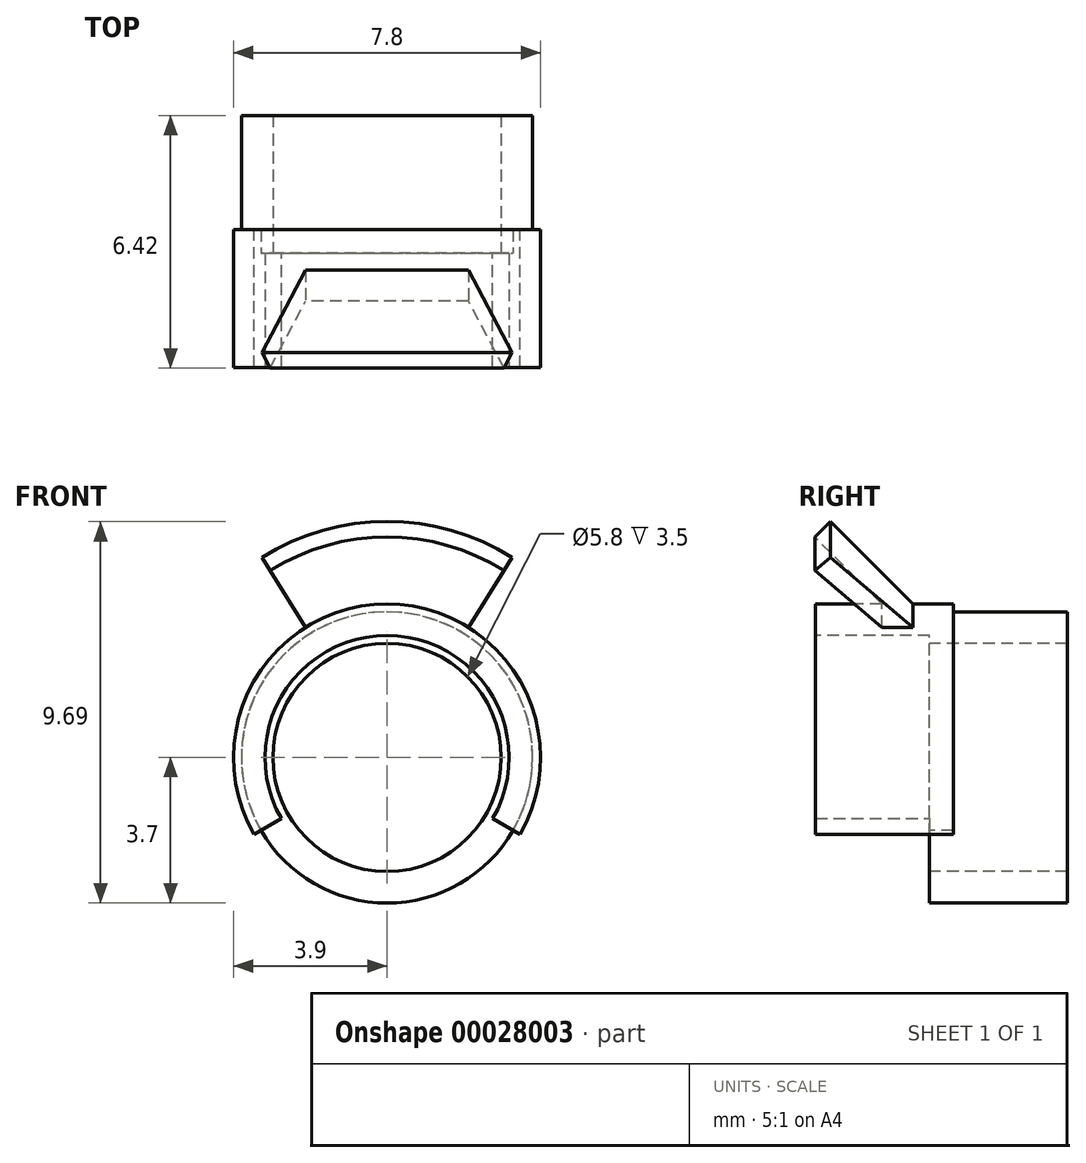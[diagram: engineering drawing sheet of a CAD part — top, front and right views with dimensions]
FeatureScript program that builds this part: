
annotation { "Feature Type Name" : "Feature", "Feature Type Description" : "" }
export const myFeature = defineFeature(function(context is Context, id is Id, definition is map)
    precondition{}
    {
        {
            var Q0;
            Q0=qCreatedBy(makeId("Right.planeOp"),FACE);
            var sketch = newSketch(context, id + "F0", { "sketchPlane" : qUnion([Q0])});
            skLineSegment(sketch, "E0.bottom", {"start": v(0.1, 3.9) * mm, "end": v(3.6, 3.9) * mm});
            skLineSegment(sketch, "E0.top", {"start": v(0.1, 3.1) * mm, "end": v(3.6, 3.1) * mm});
            skLineSegment(sketch, "E0.left", {"start": v(0.1, 3.9) * mm, "end": v(0.1, 3.1) * mm});
            skLineSegment(sketch, "E0.right", {"start": v(3.6, 3.9) * mm, "end": v(3.6, 3.1) * mm});
            skLineSegment(sketch, "E1.bottom", {"start": v(0.1, 3.1) * mm, "end": v(1.3, 3.1) * mm});
            skLineSegment(sketch, "E1.top", {"start": v(0.1, 2.3) * mm, "end": v(1.3, 2.3) * mm});
            skLineSegment(sketch, "E1.left", {"start": v(0.1, 3.1) * mm, "end": v(0.1, 2.3) * mm});
            skLineSegment(sketch, "E1.right", {"start": v(1.3, 3.1) * mm, "end": v(1.3, 2.3) * mm});
            skLineSegment(sketch, "E2", {"start": v(1.3, 3.1) * mm, "end": v(3.6, 3.1) * mm});
            skLineSegment(sketch, "E3", {"start": v(0.7, 2.3) * mm, "end": v(0.7, 0) * mm});
            skLineSegment(sketch, "E4", {"start": v(-8.7, 0) * mm, "end": v(0, 0) * mm});
            skLineSegment(sketch, "E5", {"start": v(0.1, 3.1) * mm, "end": v(0.1, 3.9) * mm});
            skLineSegment(sketch, "E6", {"start": v(-9.9, 0) * mm, "end": v(-3.58, 0) * mm});
            skLineSegment(sketch, "E7", {"start": v(0, 0) * mm, "end": v(0.7, 0) * mm});
            skLineSegment(sketch, "E8", {"start": v(0.7, 0) * mm, "end": v(0, 0) * mm});
            skSolve(sketch);
        }
        {
            var Q0;
            Q0=makeQuery(id+"F0.imprint","IMPRINT",FACE,{"disambiguationData":[TD([[makeQuery(id+"F0.imprint","IMPRINT",EDGE,{"derivedFrom":sQuery(id+"F0.wireOp",EDGE,"E1.bottom")}),-1.0]])]});
            var Q1;
            Q1=makeQuery(id+"F0.imprint","IMPRINT",FACE,{"disambiguationData":[TD([[makeQuery(id+"F0.imprint","IMPRINT",EDGE,{"derivedFrom":sQuery(id+"F0.wireOp",EDGE,"E0.bottom")}),-1.0]])]});
            var Q2;
            Q2=sQuery(id+"F0.wireOp",EDGE,"E4");
            revolve(context, id + "F1", {"entities" : qUnion([Q0, Q1]), "axis" : qUnion([Q2]), "revolveType" : RevolveType.TWO_DIRECTIONS, "angle" : 120 * degree, "angleBack" : 240 * degree});
        }
        {
            var Q0;
            Q0=qCreatedBy(makeId("Right.planeOp"),FACE);
            var sketch = newSketch(context, id + "F2", { "sketchPlane" : qUnion([Q0])});
            skLineSegment(sketch, "E9", {"start": v(2.6, 3.87) * mm, "end": v(0.48, 6) * mm});
            skLineSegment(sketch, "E10", {"start": v(0.48, 6) * mm, "end": v(0.08, 5.6) * mm});
            skLineSegment(sketch, "E11", {"start": v(0.08, 5.6) * mm, "end": v(2.61, 3.07) * mm});
            skLineSegment(sketch, "E12", {"start": v(2.61, 3.07) * mm, "end": v(2.6, 3.87) * mm});
            skLineSegment(sketch, "E13", {"start": v(0, 3.87) * mm, "end": v(2.6, 3.87) * mm});
            skLineSegment(sketch, "E14", {"start": v(-6.62, 0) * mm, "end": v(0, 0) * mm});
            skLineSegment(sketch, "E15", {"start": v(0.08, 5.6) * mm, "end": v(0.08, 0) * mm});
            skSolve(sketch);
        }
        {
            var Q0;
            Q0=makeQuery(id+"F2.imprint","IMPRINT",FACE,{"disambiguationData":[TD([[makeQuery(id+"F2.imprint","IMPRINT",EDGE,{"derivedFrom":sQuery(id+"F2.wireOp",EDGE,"E9")}),1.0]])]});
            var Q1;
            Q1=sQuery(id+"F2.wireOp",EDGE,"E14");
            revolve(context, id + "F3", {"operationType" : NewBodyOperationType.ADD, "entities" : qUnion([Q0]), "axis" : qUnion([Q1]), "revolveType" : RevolveType.TWO_DIRECTIONS, "angle" : 32 * degree, "angleBack" : 328 * degree});
        }
        {
            var Q0;
            Q0=qCreatedBy(makeId("Right.planeOp"),FACE);
            var sketch = newSketch(context, id + "F4", { "sketchPlane" : qUnion([Q0])});
            skLineSegment(sketch, "E16.bottom", {"start": v(3, 3.7) * mm, "end": v(6.5, 3.7) * mm});
            skLineSegment(sketch, "E16.top", {"start": v(3, 2.9) * mm, "end": v(6.5, 2.9) * mm});
            skLineSegment(sketch, "E16.left", {"start": v(3, 3.7) * mm, "end": v(3, 2.9) * mm});
            skLineSegment(sketch, "E16.right", {"start": v(6.5, 3.7) * mm, "end": v(6.5, 2.9) * mm});
            skLineSegment(sketch, "E17", {"start": v(0, 0) * mm, "end": v(3.41, 0) * mm});
            skLineSegment(sketch, "E18", {"start": v(0, 3.62) * mm, "end": v(3, 3.62) * mm});
            skLineSegment(sketch, "E19", {"start": v(2.4, 2.9) * mm, "end": v(2.4, 0) * mm});
            skSolve(sketch);
        }
        {
            var Q0;
            Q0=makeQuery(id+"F4.imprint","IMPRINT",FACE,{"disambiguationData":[TD([[makeQuery(id+"F4.imprint","IMPRINT",EDGE,{"derivedFrom":sQuery(id+"F4.wireOp",EDGE,"E16.bottom")}),-1.0]])]});
            var Q1;
            Q1=sQuery(id+"F4.wireOp",EDGE,"E17");
            revolve(context, id + "F5", {"operationType" : NewBodyOperationType.ADD, "entities" : qUnion([Q0]), "axis" : qUnion([Q1]), "revolveType" : RevolveType.FULL});
        }
    });
